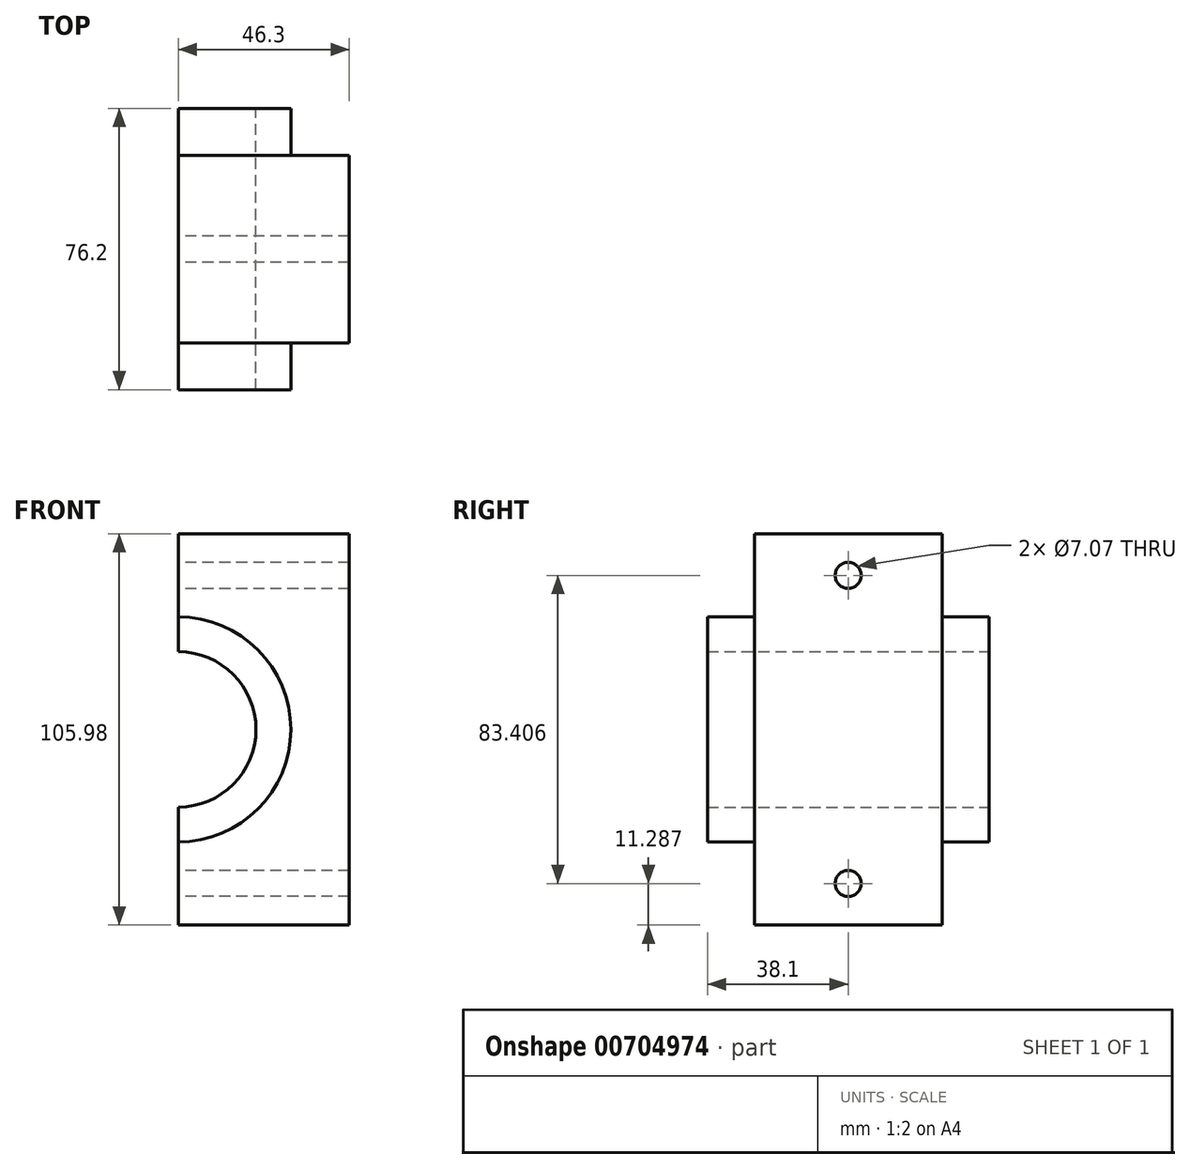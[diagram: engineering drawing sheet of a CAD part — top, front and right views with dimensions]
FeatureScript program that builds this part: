
annotation { "Feature Type Name" : "Feature", "Feature Type Description" : "" }
export const myFeature = defineFeature(function(context is Context, id is Id, definition is map)
    precondition{}
    {
        {
            var Q0;
            Q0=qCreatedBy(makeId("Front.planeOp"),FACE);
            var sketch = newSketch(context, id + "F0", { "sketchPlane" : qUnion([Q0])});
            skArc(sketch, "E0", {"start": v(0, -21.04) * mm, "mid": v(21.04, 0) * mm, "end": v(0, 21.04) * mm});
            skArc(sketch, "E1", {"start": v(0, -30.47) * mm, "mid": v(30.47, 0) * mm, "end": v(0, 30.47) * mm});
            skLineSegment(sketch, "E2", {"start": v(0, 21.04) * mm, "end": v(0, 53) * mm});
            skLineSegment(sketch, "E3", {"start": v(0, 53) * mm, "end": v(46.3, 53) * mm});
            skLineSegment(sketch, "E4", {"start": v(46.3, 53) * mm, "end": v(46.3, 0) * mm});
            skLineSegment(sketch, "E5.MirrorCS", {"start": v(46.3, -53) * mm, "end": v(46.3, 0) * mm});
            skLineSegment(sketch, "E6.MirrorCS", {"start": v(0, -53) * mm, "end": v(46.3, -53) * mm});
            skLineSegment(sketch, "E7.MirrorCS", {"start": v(0, -21.04) * mm, "end": v(0, -53) * mm});
            skSolve(sketch);
        }
        {
            var Q0;
            Q0 = qSketchRegion(id + "F0", true);
            extrude(context, id + "F1", {"entities" : qUnion([Q0]), "depth" : 25.4 * mm, "offsetDistance" : 25.4 * mm, "hasSecondDirection" : true, "secondDirectionOppositeDirection" : true, "secondDirectionDepth" : 25.4 * mm});
        }
        {
            var Q0;
            {var subQ0=sQuery(id+"F0.wireOp",EDGE,"E0");Q0=makeQuery(id+"F0.imprint","IMPRINT",FACE,{"disambiguationData":[TD([[makeQuery(id+"F0.imprint","IMPRINT",EDGE,{"derivedFrom":subQ0}),-1.0]])]});}
            extrude(context, id + "F2", {"entities" : qUnion([Q0]), "operationType" : NewBodyOperationType.ADD, "depth" : 38.1 * mm, "offsetDistance" : 25.4 * mm, "hasSecondDirection" : true, "secondDirectionOppositeDirection" : true, "secondDirectionDepth" : 38.1 * mm});
        }
        {
            var Q0;
            Q0=qCreatedBy(makeId("Right.planeOp"),FACE);
            var sketch = newSketch(context, id + "F3", { "sketchPlane" : qUnion([Q0])});
            skCircle(sketch, "E8", {"center": v(0, -41.7) * mm, "radius": 3.53 * mm});
            skCircle(sketch, "E9.MirrorC", {"center": v(0, 41.7) * mm, "radius": 3.53 * mm});
            skSolve(sketch);
        }
        {
            var Q0;
            Q0 = qSketchRegion(id + "F3", true);
            extrude(context, id + "F4", {"entities" : qUnion([Q0]), "operationType" : NewBodyOperationType.REMOVE, "endBound" : BoundingType.THROUGH_ALL, "depth" : 25.4 * mm, "offsetDistance" : 25.4 * mm});
        }
    });
